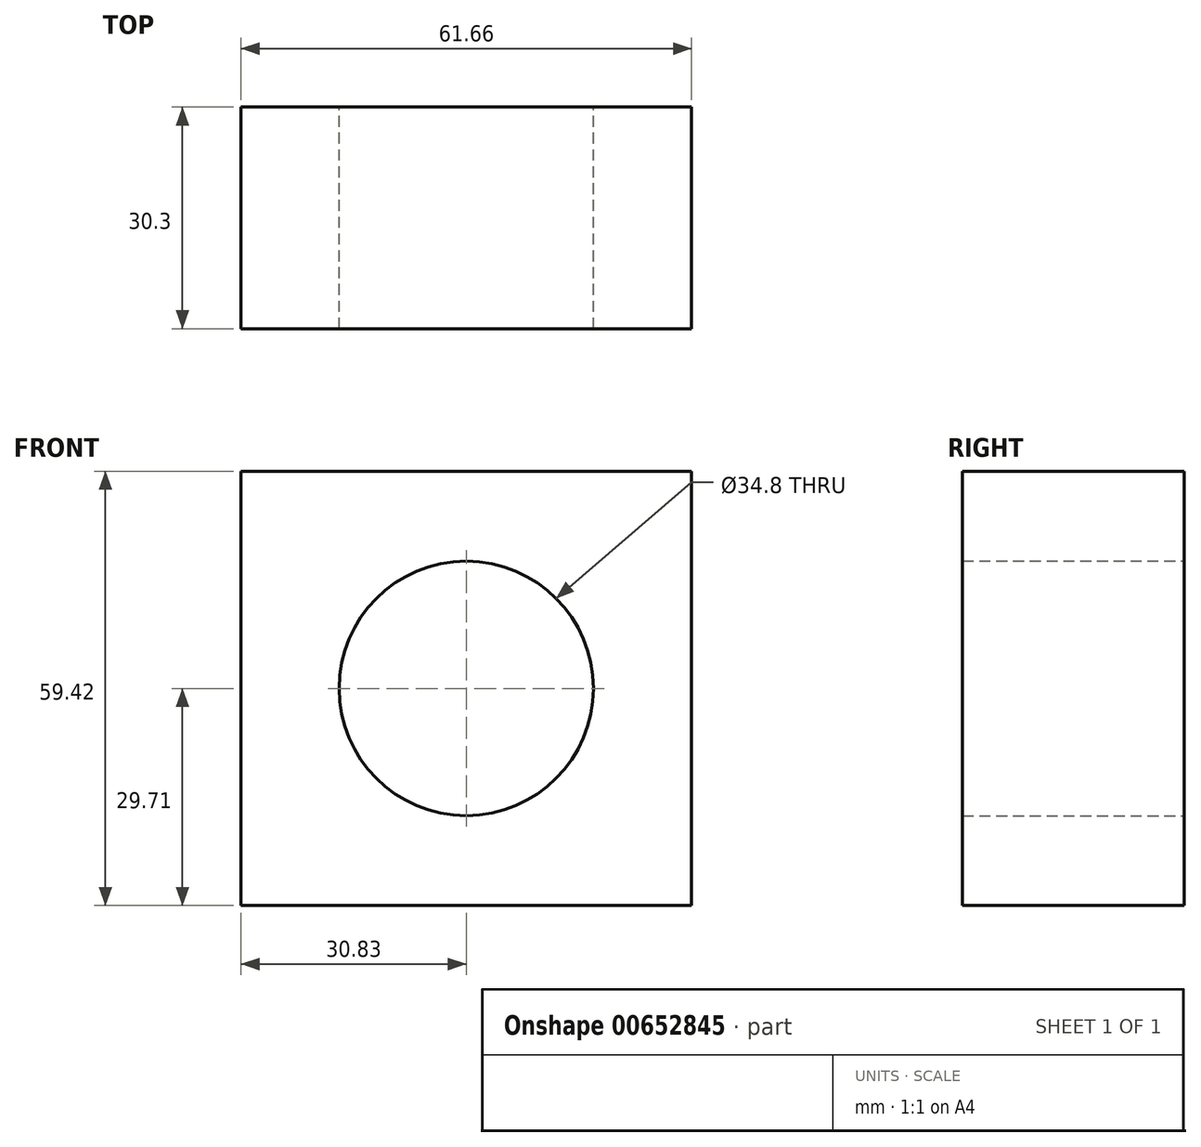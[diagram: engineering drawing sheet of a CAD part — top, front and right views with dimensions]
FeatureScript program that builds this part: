
annotation { "Feature Type Name" : "Feature", "Feature Type Description" : "" }
export const myFeature = defineFeature(function(context is Context, id is Id, definition is map)
    precondition{}
    {
        {
            var Q0;
            Q0=qCreatedBy(makeId("Front.planeOp"),FACE);
            var sketch = newSketch(context, id + "F0", { "sketchPlane" : qUnion([Q0])});
            skLineSegment(sketch, "E0.bottom", {"start": v(-30.82, 29.72) * mm, "end": v(30.83, 29.72) * mm});
            skLineSegment(sketch, "E0.top", {"start": v(-30.83, -29.72) * mm, "end": v(30.82, -29.72) * mm});
            skLineSegment(sketch, "E0.left", {"start": v(-30.82, 29.72) * mm, "end": v(-30.83, -29.72) * mm});
            skLineSegment(sketch, "E0.right", {"start": v(30.83, 29.72) * mm, "end": v(30.82, -29.72) * mm});
            skPoint(sketch, "E0.middle", {"position": v(0, 0) * mm});
            skCircle(sketch, "E1", {"center": v(0, 0) * mm, "radius": 17.4 * mm});
            skSolve(sketch);
        }
        {
            var Q0;
            Q0=makeQuery(id+"F0.imprint","IMPRINT",FACE,{"disambiguationData":[TD([[makeQuery(id+"F0.imprint","IMPRINT",EDGE,{"derivedFrom":sQuery(id+"F0.wireOp",EDGE,"E0.bottom")}),-1.0]])]});
            extrude(context, id + "F1", {"entities" : qUnion([Q0]), "depth" : 30.3 * mm, "offsetDistance" : 25 * mm});
        }
    });
